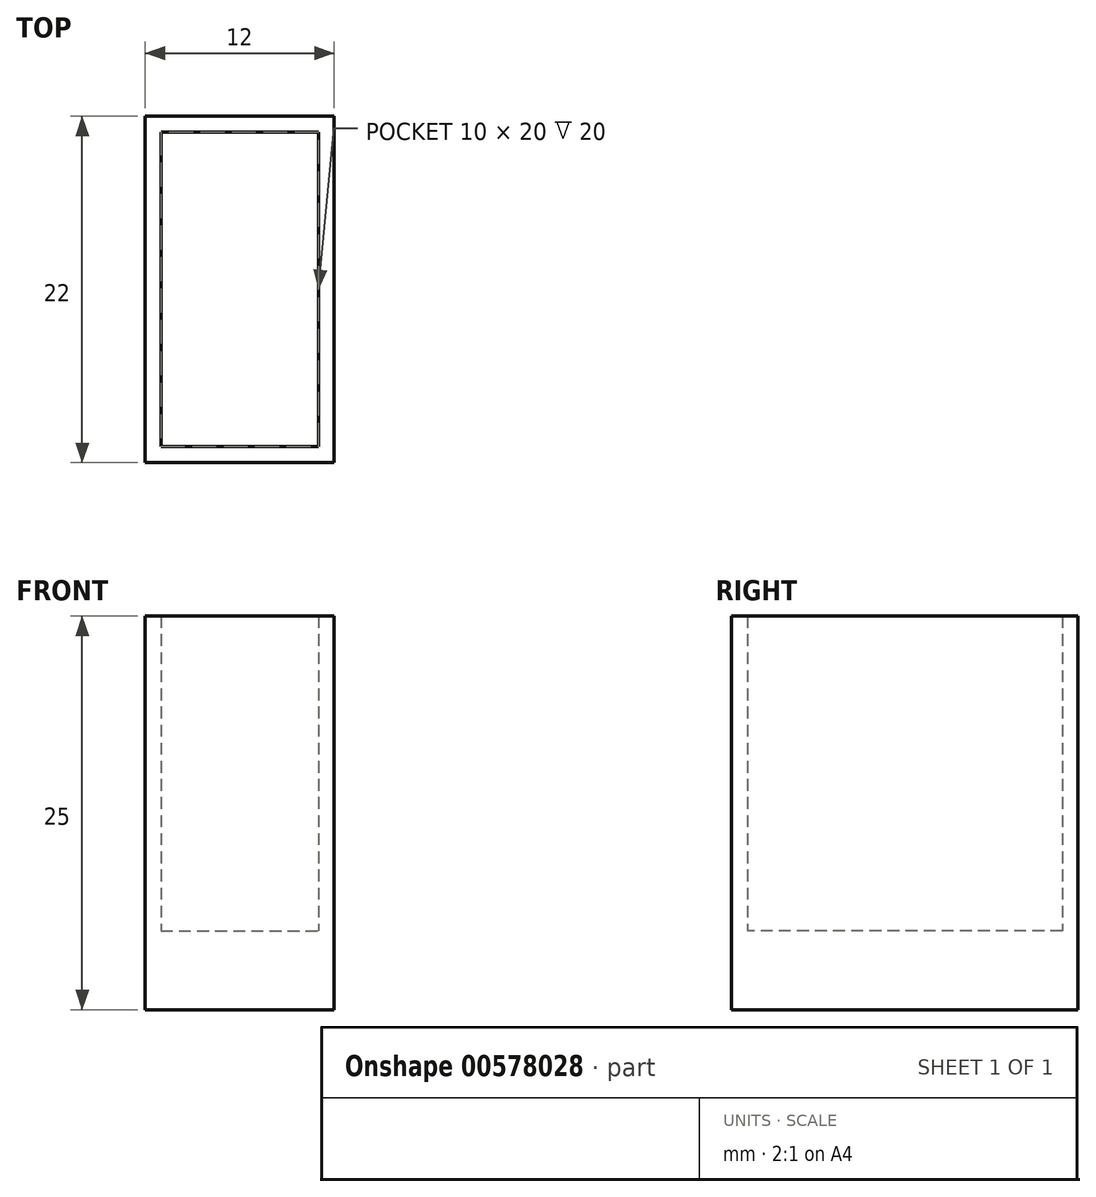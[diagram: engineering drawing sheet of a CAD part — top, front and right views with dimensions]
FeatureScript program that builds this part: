
annotation { "Feature Type Name" : "Feature", "Feature Type Description" : "" }
export const myFeature = defineFeature(function(context is Context, id is Id, definition is map)
    precondition{}
    {
        {
            var Q0;
            Q0=qCreatedBy(makeId("Top.planeOp"),FACE);
            var sketch = newSketch(context, id + "F0", { "sketchPlane" : qUnion([Q0])});
            skLineSegment(sketch, "E0.bottom", {"start": v(-164.78, -12.43) * mm, "end": v(-176.78, -12.43) * mm});
            skLineSegment(sketch, "E0.top", {"start": v(-164.78, 9.57) * mm, "end": v(-176.78, 9.57) * mm});
            skLineSegment(sketch, "E0.left", {"start": v(-164.78, -12.43) * mm, "end": v(-164.78, 9.57) * mm});
            skLineSegment(sketch, "E0.right", {"start": v(-176.78, -12.43) * mm, "end": v(-176.78, 9.57) * mm});
            skPoint(sketch, "E0.middle", {"position": v(-170.78, -1.43) * mm});
            skLineSegment(sketch, "E1.bottom", {"start": v(-165.78, -11.43) * mm, "end": v(-175.78, -11.43) * mm});
            skLineSegment(sketch, "E1.top", {"start": v(-165.78, 8.57) * mm, "end": v(-175.78, 8.57) * mm});
            skLineSegment(sketch, "E1.left", {"start": v(-165.78, -11.43) * mm, "end": v(-165.78, 8.57) * mm});
            skLineSegment(sketch, "E1.right", {"start": v(-175.78, -11.43) * mm, "end": v(-175.78, 8.57) * mm});
            skSolve(sketch);
        }
        {
            var Q0;
            Q0=makeQuery(id+"F0.imprint","IMPRINT",FACE,{"disambiguationData":[TD([[makeQuery(id+"F0.imprint","IMPRINT",EDGE,{"derivedFrom":sQuery(id+"F0.wireOp",EDGE,"E1.bottom")}),-1.0]])]});
            var Q1;
            Q1=makeQuery(id+"F0.imprint","IMPRINT",FACE,{"disambiguationData":[TD([[makeQuery(id+"F0.imprint","IMPRINT",EDGE,{"derivedFrom":sQuery(id+"F0.wireOp",EDGE,"E1.bottom")}),1.0]])]});
            extrude(context, id + "F1", {"entities" : qUnion([Q0, Q1]), "depth" : 5 * mm, "offsetDistance" : 25 * mm});
        }
        {
            var Q0;
            Q0 = qSketchRegion(id + "F0", true);
            extrude(context, id + "F2", {"entities" : qUnion([Q0]), "operationType" : NewBodyOperationType.ADD, "depth" : 25 * mm, "offsetDistance" : 25 * mm});
        }
    });
